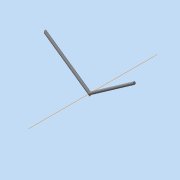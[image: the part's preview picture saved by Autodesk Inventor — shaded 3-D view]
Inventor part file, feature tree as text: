
AUTODESK INVENTOR PART (.ipt)
format: ipt  version: 2019.4 (Build 234330000, 330)  size: 113,152 bytes
history: native  units: mm
features: other x4, sketch x3, reference x3, plane x1, sweep x1, extrude x1, projected_geometry x1
ambient origin geometry x8: Origin, YZ Plane, XZ Plane, XY Plane, X Axis, Y Axis, Z Axis, Center Point
bodies: Body1 (feature_tree)
feature tree (14):
  sketch  "Sketch1"  dims[d3=0.0mm d19=9.599311mm]
  plane  "Work Plane3"
  sweep  "Sweep2"
  extrude  "Extrusion3"  Depth=24.0mm
  reference  "Reference1"
  reference  "Reference2"
  sketch  "Sketch5"  dims[d20=24.0mm d21=24.0mm]
  sketch  "Sketch6"  dims[d22=2.0mm d23=0.0mm d24=0.0mm d26=3.0mm d27=0.0mm d28=1.0mm d29=1.0mm]
  reference  "Reference4"
  projected_geometry  "Projected Loop2"
  other  "Assembly_Opentrons_Autofocus_Measure_v0.iam"
  other  "00_ESP32_CAM:1"
  other  "Assembly_Opentrons_Autofocus_v1.iam"
  other  "08_Opentrons_Autofocus_flexurebaering:1"
